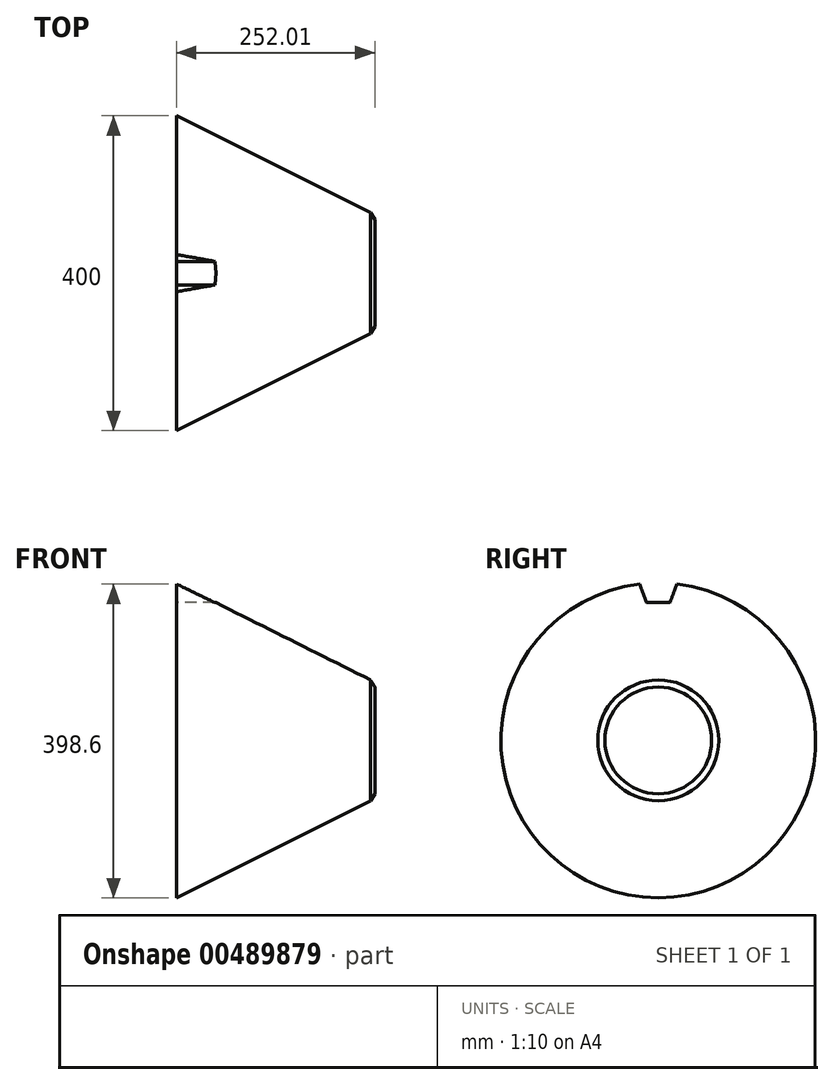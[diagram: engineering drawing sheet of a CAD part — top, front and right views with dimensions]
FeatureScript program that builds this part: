
annotation { "Feature Type Name" : "Feature", "Feature Type Description" : "" }
export const myFeature = defineFeature(function(context is Context, id is Id, definition is map)
    precondition{}
    {
        {
            var Q0;
            Q0=qCreatedBy(makeId("Front.planeOp"),FACE);
            var sketch = newSketch(context, id + "F0", { "sketchPlane" : qUnion([Q0])});
            skLineSegment(sketch, "E0", {"start": v(0, 0) * mm, "end": v(0, 200) * mm});
            skLineSegment(sketch, "E1", {"start": v(0, 0) * mm, "end": v(400, 0) * mm});
            skLineSegment(sketch, "E2", {"start": v(-112.68, 0) * mm, "end": v(494.81, 0) * mm, "construction": true});
            skLineSegment(sketch, "E3", {"start": v(252.01, 74) * mm, "end": v(252.01, 0) * mm});
            skLineSegment(sketch, "E4", {"start": v(252.01, 74) * mm, "end": v(0, 200) * mm});
            skSolve(sketch);
        }
        {
            var Q0;
            {var subQ0=sQuery(id+"F0.wireOp",EDGE,"E0");Q0=makeQuery(id+"F0.imprint","IMPRINT",FACE,{"disambiguationData":[TD([[makeQuery(id+"F0.imprint","IMPRINT",EDGE,{"derivedFrom":subQ0}),-1.0]])]});}
            var Q1;
            Q1=sQuery(id+"F0.wireOp",EDGE,"E2");
            revolve(context, id + "F1", {"entities" : qUnion([Q0]), "axis" : qUnion([Q1]), "revolveType" : RevolveType.FULL});
        }
        {
            var Q0;
            Q0=makeQuery(id+"F1.opRevolve","SWEPT_EDGE",EDGE,{"disambiguationData":[OSD([sQuery(id+"F0.wireOp",EDGE,"E3"),sQuery(id+"F0.wireOp",EDGE,"E4")])]});
            chamfer(context, id + "F2", {"entities" : qUnion([Q0]), "width" : 10 * mm, "tangentPropagation" : true});
        }
        {
            var Q0;
            Q0=makeQuery(id+"F1.opRevolve","SWEPT_FACE",FACE,{"disambiguationData":[OSD([sQuery(id+"F0.wireOp",EDGE,"E0")])]});
            var sketch = newSketch(context, id + "F3", { "sketchPlane" : qUnion([Q0])});
            skLineSegment(sketch, "E5", {"start": v(0, 0) * mm, "end": v(0, 200) * mm, "construction": true});
            skLineSegment(sketch, "E6", {"start": v(0, 175) * mm, "end": v(15, 175) * mm});
            skLineSegment(sketch, "E7", {"start": v(0, 175) * mm, "end": v(-15, 175) * mm});
            skLineSegment(sketch, "E8", {"start": v(-15, 175) * mm, "end": v(-23.6, 198.6) * mm});
            skLineSegment(sketch, "E9", {"start": v(15, 175) * mm, "end": v(23.6, 198.6) * mm});
            skSolve(sketch);
        }
        {
            var Q0;
            Q0=makeQuery(id+"F3.imprint","IMPRINT",FACE,{"disambiguationData":[TD([[makeQuery(id+"F3.imprint","IMPRINT",EDGE,{"derivedFrom":sQuery(id+"F3.wireOp",EDGE,"E6")}),1.0]])]});
            extrude(context, id + "F4", {"entities" : qUnion([Q0]), "operationType" : NewBodyOperationType.REMOVE, "oppositeDirection" : true, "depth" : 1000 * mm});
        }
    });
